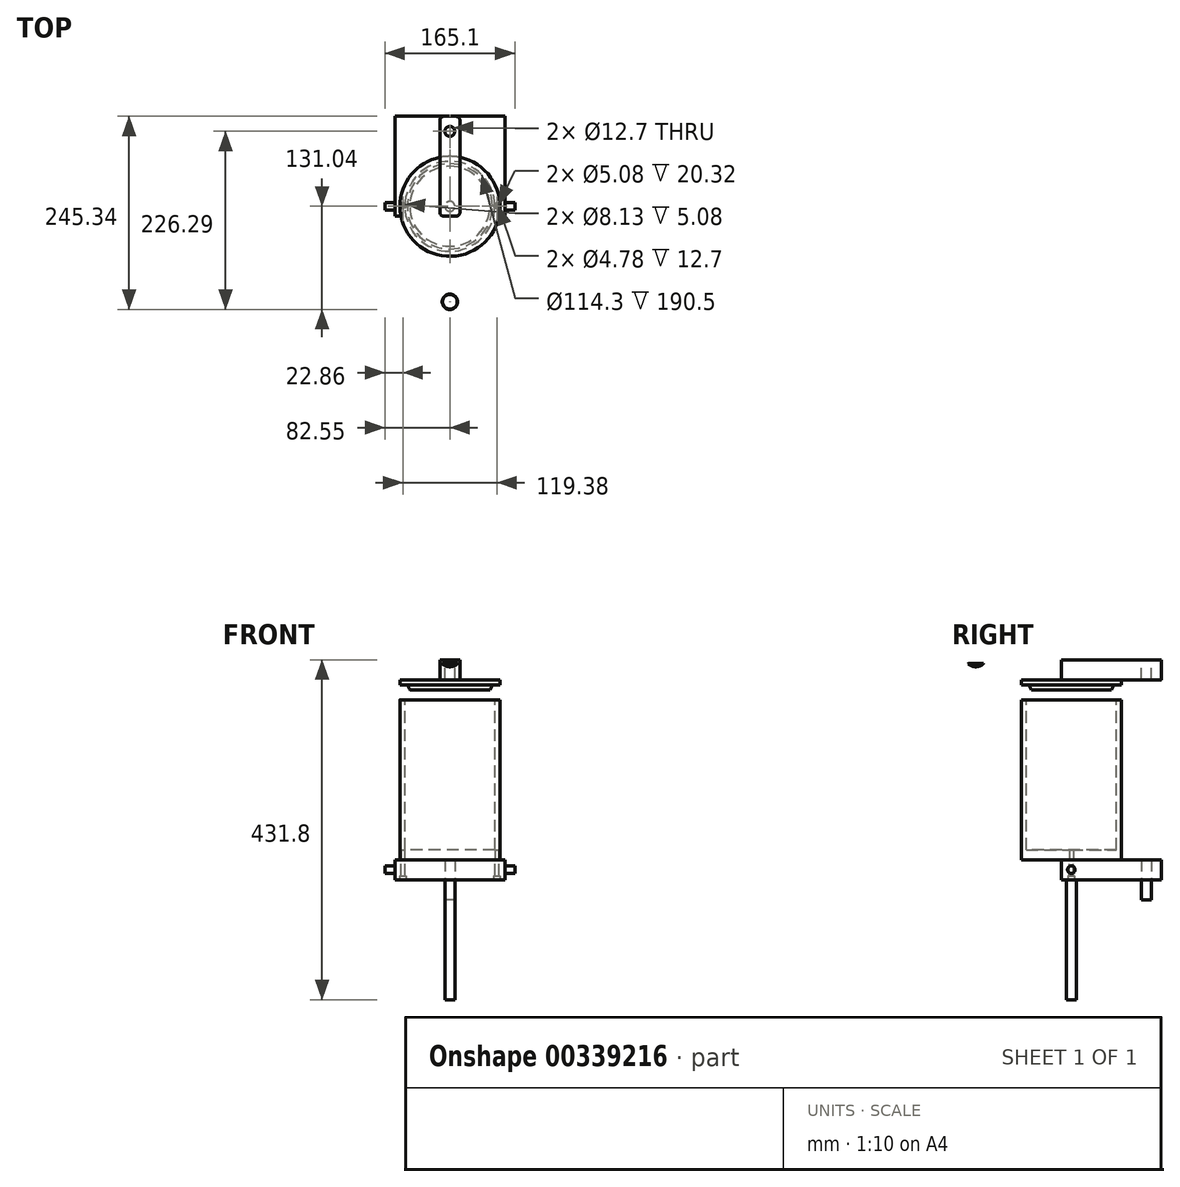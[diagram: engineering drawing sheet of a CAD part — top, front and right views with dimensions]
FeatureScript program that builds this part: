
annotation { "Feature Type Name" : "Feature", "Feature Type Description" : "" }
export const myFeature = defineFeature(function(context is Context, id is Id, definition is map)
    precondition{}
    {
        {
            var Q0;
            Q0=qCreatedBy(makeId("Top.planeOp"),FACE);
            var sketch = newSketch(context, id + "F0", { "sketchPlane" : qUnion([Q0])});
            skCircle(sketch, "E0", {"center": v(0, 0) * mm, "radius": 63.5 * mm});
            skSolve(sketch);
        }
        {
            var Q0;
            Q0=qSketchRegion(id+"F0",true);
            extrude(context, id + "F1", {"entities" : qUnion([Q0]), "depth" : 203.2 * mm});
        }
        {
            var Q0;
            Q0=makeQuery(id+"F1.opExtrude","CAP_FACE",FACE,{"disambiguationData":[OSD([sQuery(id+"F0.wireOp",EDGE,"E0")])],"isStart":false});
            var sketch = newSketch(context, id + "F2", { "sketchPlane" : qUnion([Q0])});
            skCircle(sketch, "E1", {"center": v(0, 0) * mm, "radius": 57.15 * mm});
            skSolve(sketch);
        }
        {
            var Q0;
            Q0=qSketchRegion(id+"F2",true);
            extrude(context, id + "F3", {"entities" : qUnion([Q0]), "operationType" : NewBodyOperationType.REMOVE, "oppositeDirection" : true, "depth" : 190.5 * mm});
        }
        {
            var Q0;
            Q0=qCreatedBy(makeId("Top.planeOp"),FACE);
            cPlane(context, id + "F4", {"entities" : qUnion([Q0]), "cplaneType" : CPlaneType.OFFSET, "offset" : 254 * mm, "width" : 152.4 * mm, "height" : 152.4 * mm});
        }
        {
            var Q0;
            Q0=qCreatedBy(makeId("Front.planeOp"),FACE);
            var sketch = newSketch(context, id + "F5", { "sketchPlane" : qUnion([Q0])});
            skLineSegment(sketch, "E2", {"start": v(0, 228.6) * mm, "end": v(-63.5, 228.6) * mm});
            skLineSegment(sketch, "E3", {"start": v(-63.5, 228.6) * mm, "end": v(-63.5, 222.25) * mm});
            skLineSegment(sketch, "E4", {"start": v(-63.5, 222.25) * mm, "end": v(-54.11, 222.25) * mm});
            skLineSegment(sketch, "E5", {"start": v(-54.11, 222.25) * mm, "end": v(-50.8, 215.9) * mm});
            skLineSegment(sketch, "E6", {"start": v(-50.8, 215.9) * mm, "end": v(0, 215.9) * mm});
            skLineSegment(sketch, "E7", {"start": v(0, 215.9) * mm, "end": v(0, 228.6) * mm});
            skSolve(sketch);
        }
        {
            var Q0;
            Q0=qSketchRegion(id+"F5",true);
            var Q1;
            Q1=sQuery(id+"F5.wireOp",EDGE,"E7");
            revolve(context, id + "F6", {"entities" : qUnion([Q0]), "axis" : qUnion([Q1]), "revolveType" : RevolveType.FULL});
        }
        {
            var Q0;
            Q0=makeQuery(id+"F1.opExtrude","CAP_FACE",FACE,{"disambiguationData":[OSD([sQuery(id+"F0.wireOp",EDGE,"E0")])],"isStart":true});
            var sketch = newSketch(context, id + "F7", { "sketchPlane" : qUnion([Q0])});
            skCircle(sketch, "E8", {"center": v(-59.7, 0) * mm, "radius": 2.39 * mm});
            skCircle(sketch, "E9", {"center": v(59.7, 0) * mm, "radius": 2.39 * mm});
            skSolve(sketch);
        }
        {
            var Q0;
            Q0=qSketchRegion(id+"F7",true);
            extrude(context, id + "F8", {"entities" : qUnion([Q0]), "operationType" : NewBodyOperationType.REMOVE, "oppositeDirection" : true, "depth" : 12.7 * mm});
        }
        {
            var Q0;
            Q0=makeQuery(id+"F1.opExtrude","CAP_FACE",FACE,{"disambiguationData":[OSD([sQuery(id+"F0.wireOp",EDGE,"E0")])],"isStart":true});
            var sketch = newSketch(context, id + "F9", { "sketchPlane" : qUnion([Q0])});
            skLineSegment(sketch, "E10.bottom", {"start": v(69.85, 12.7) * mm, "end": v(-69.85, 12.7) * mm});
            skLineSegment(sketch, "E10.top", {"start": v(69.85, -12.7) * mm, "end": v(-69.85, -12.7) * mm});
            skLineSegment(sketch, "E10.left", {"start": v(69.85, 12.7) * mm, "end": v(69.85, -12.7) * mm});
            skLineSegment(sketch, "E10.right", {"start": v(-69.85, 12.7) * mm, "end": v(-69.85, -12.7) * mm});
            skPoint(sketch, "E10.middle", {"position": v(0, 0) * mm});
            skCircle(sketch, "E11", {"center": v(-59.7, 0) * mm, "radius": 2.54 * mm});
            skCircle(sketch, "E12", {"center": v(59.7, 0) * mm, "radius": 2.54 * mm});
            skSolve(sketch);
        }
        {
            var Q0;
            Q0=qSketchRegion(id+"F9",true);
            extrude(context, id + "F10", {"entities" : qUnion([Q0]), "depth" : 25.4 * mm});
        }
        {
            var Q0;
            Q0=makeQuery(id+"F10.opExtrude","CAP_FACE",FACE,{"disambiguationData":[OSD([sQuery(id+"F9.wireOp",EDGE,"E10.bottom"),sQuery(id+"F9.wireOp",EDGE,"E10.top"),sQuery(id+"F9.wireOp",EDGE,"E10.left"),sQuery(id+"F9.wireOp",EDGE,"E10.right"),sQuery(id+"F9.wireOp",EDGE,"E11"),sQuery(id+"F9.wireOp",EDGE,"E12")])],"isStart":false});
            var sketch = newSketch(context, id + "F11", { "sketchPlane" : qUnion([Q0])});
            skCircle(sketch, "E13", {"center": v(-59.7, 0) * mm, "radius": 4.06 * mm});
            skCircle(sketch, "E14", {"center": v(59.7, 0) * mm, "radius": 4.06 * mm});
            skSolve(sketch);
        }
        {
            var Q0;
            Q0=qSketchRegion(id+"F11",true);
            extrude(context, id + "F12", {"entities" : qUnion([Q0]), "operationType" : NewBodyOperationType.REMOVE, "oppositeDirection" : true, "depth" : 5.08 * mm});
        }
        {
            var Q0;
            Q0=makeQuery(id+"F10.opExtrude","SWEPT_FACE",FACE,{"disambiguationData":[OSD([sQuery(id+"F9.wireOp",EDGE,"E10.right")])]});
            var sketch = newSketch(context, id + "F13", { "sketchPlane" : qUnion([Q0])});
            skCircle(sketch, "E15", {"center": v(0, -12.7) * mm, "radius": 4.76 * mm});
            skSolve(sketch);
        }
        {
            var Q0;
            Q0=makeQuery(id+"F10.opExtrude","CAP_FACE",FACE,{"disambiguationData":[OSD([sQuery(id+"F9.wireOp",EDGE,"E10.bottom"),sQuery(id+"F9.wireOp",EDGE,"E10.top"),sQuery(id+"F9.wireOp",EDGE,"E10.left"),sQuery(id+"F9.wireOp",EDGE,"E10.right"),sQuery(id+"F9.wireOp",EDGE,"E11"),sQuery(id+"F9.wireOp",EDGE,"E12")])],"isStart":false});
            var sketch = newSketch(context, id + "F14", { "sketchPlane" : qUnion([Q0])});
            skCircle(sketch, "E16", {"center": v(0, 0) * mm, "radius": 6.35 * mm});
            skSolve(sketch);
        }
        {
            var Q0;
            Q0=qSketchRegion(id+"F14",true);
            extrude(context, id + "F15", {"entities" : qUnion([Q0]), "depth" : 152.4 * mm});
        }
        {
            var Q0;
            Q0=makeQuery(id+"F6.opRevolve","SWEPT_FACE",FACE,{"disambiguationData":[OSD([sQuery(id+"F5.wireOp",EDGE,"E2")])]});
            var sketch = newSketch(context, id + "F16", { "sketchPlane" : qUnion([Q0])});
            skLineSegment(sketch, "E17.bottom", {"start": v(12.7, -12.7) * mm, "end": v(-12.7, -12.7) * mm});
            skLineSegment(sketch, "E17.top", {"start": v(12.7, 114.3) * mm, "end": v(-12.7, 114.3) * mm});
            skLineSegment(sketch, "E17.left", {"start": v(12.7, -12.7) * mm, "end": v(12.7, 114.3) * mm});
            skLineSegment(sketch, "E17.right", {"start": v(-12.7, -12.7) * mm, "end": v(-12.7, 114.3) * mm});
            skSolve(sketch);
        }
        {
            var Q0;
            Q0=qSketchRegion(id+"F16",true);
            extrude(context, id + "F17", {"entities" : qUnion([Q0]), "depth" : 25.4 * mm});
        }
        {
            var Q0;
            Q0=makeQuery(id+"F17.opExtrude","CAP_FACE",FACE,{"disambiguationData":[OSD([sQuery(id+"F16.wireOp",EDGE,"E17.bottom"),sQuery(id+"F16.wireOp",EDGE,"E17.top"),sQuery(id+"F16.wireOp",EDGE,"E17.left"),sQuery(id+"F16.wireOp",EDGE,"E17.right")])],"isStart":false});
            var sketch = newSketch(context, id + "F18", { "sketchPlane" : qUnion([Q0])});
            skCircle(sketch, "E18", {"center": v(0, 95.25) * mm, "radius": 6.35 * mm});
            skSolve(sketch);
        }
        {
            var Q0;
            Q0=qSketchRegion(id+"F18",true);
            extrude(context, id + "F19", {"entities" : qUnion([Q0]), "operationType" : NewBodyOperationType.REMOVE, "oppositeDirection" : true, "depth" : 25.4 * mm});
        }
        {
            var Q0;
            Q0=qCreatedBy(id+"F4.planeOp",FACE);
            var sketch = newSketch(context, id + "F20", { "sketchPlane" : qUnion([Q0])});
            skCircle(sketch, "E19", {"center": v(0, 95.25) * mm, "radius": 6.35 * mm});
            skSolve(sketch);
        }
        {
            var Q0;
            Q0=qSketchRegion(id+"F20",true);
            extrude(context, id + "F21", {"entities" : qUnion([Q0]), "oppositeDirection" : true, "depth" : 304.8 * mm});
        }
        {
            var Q0;
            Q0=makeQuery(id+"F17.opExtrude","SWEPT_EDGE",EDGE,{"disambiguationData":[OSD([sQuery(id+"F16.wireOp",EDGE,"E17.bottom"),sQuery(id+"F16.wireOp",EDGE,"E17.right")])]});
            var Q1;
            Q1=makeQuery(id+"F17.opExtrude","SWEPT_EDGE",EDGE,{"disambiguationData":[OSD([sQuery(id+"F16.wireOp",EDGE,"E17.bottom"),sQuery(id+"F16.wireOp",EDGE,"E17.left")])]});
            var Q2;
            Q2=makeQuery(id+"F17.opExtrude","SWEPT_EDGE",EDGE,{"disambiguationData":[OSD([sQuery(id+"F16.wireOp",EDGE,"E17.top"),sQuery(id+"F16.wireOp",EDGE,"E17.left")])]});
            var Q3;
            Q3=makeQuery(id+"F17.opExtrude","SWEPT_EDGE",EDGE,{"disambiguationData":[OSD([sQuery(id+"F16.wireOp",EDGE,"E17.top"),sQuery(id+"F16.wireOp",EDGE,"E17.right")])]});
            fillet(context, id + "F22", {"entities" : qUnion([Q0, Q1, Q2, Q3]), "radius" : 5.08 * mm, "tangentPropagation" : true, "allowEdgeOverflow" : false});
        }
        {
            var Q0;
            Q0=makeQuery(id+"F10.opExtrude","SWEPT_FACE",FACE,{"disambiguationData":[OSD([sQuery(id+"F9.wireOp",EDGE,"E10.top")])]});
            var sketch = newSketch(context, id + "F23", { "sketchPlane" : qUnion([Q0])});
            skLineSegment(sketch, "E20.bottom", {"start": v(69.85, -25.4) * mm, "end": v(-69.85, -25.4) * mm});
            skLineSegment(sketch, "E20.top", {"start": v(69.85, 0) * mm, "end": v(-69.85, 0) * mm});
            skLineSegment(sketch, "E20.left", {"start": v(69.85, -25.4) * mm, "end": v(69.85, 0) * mm});
            skLineSegment(sketch, "E20.right", {"start": v(-69.85, -25.4) * mm, "end": v(-69.85, 0) * mm});
            skSolve(sketch);
        }
        {
            var Q0;
            Q0=qSketchRegion(id+"F23",true);
            extrude(context, id + "F24", {"entities" : qUnion([Q0]), "operationType" : NewBodyOperationType.ADD, "depth" : 101.6 * mm});
        }
        {
            var Q0;
            Q0=makeQuery(id+"F24.boolean.opBoolean","MERGE",FACE,{"derivedFrom":[makeQuery(id+"F10.opExtrude","CAP_FACE",FACE,{"disambiguationData":[OSD([sQuery(id+"F9.wireOp",EDGE,"E10.bottom"),sQuery(id+"F9.wireOp",EDGE,"E10.top"),sQuery(id+"F9.wireOp",EDGE,"E10.left"),sQuery(id+"F9.wireOp",EDGE,"E10.right"),sQuery(id+"F9.wireOp",EDGE,"E11"),sQuery(id+"F9.wireOp",EDGE,"E12")])],"isStart":false}),makeQuery(id+"F24.opExtrude","SWEPT_FACE",FACE,{"disambiguationData":[OSD([sQuery(id+"F23.wireOp",EDGE,"E20.bottom")])]})]});
            var sketch = newSketch(context, id + "F25", { "sketchPlane" : qUnion([Q0])});
            skCircle(sketch, "E21", {"center": v(0, -95.25) * mm, "radius": 6.35 * mm});
            skSolve(sketch);
        }
        {
            var Q0;
            Q0=qSketchRegion(id+"F25",true);
            extrude(context, id + "F26", {"entities" : qUnion([Q0]), "operationType" : NewBodyOperationType.REMOVE, "endBound" : BoundingType.THROUGH_ALL, "oppositeDirection" : true, "depth" : 25.4 * mm});
        }
        {
            var Q0;
            Q0=qCreatedBy(makeId("Right.planeOp"),FACE);
            var sketch = newSketch(context, id + "F27", { "sketchPlane" : qUnion([Q0])});
            skLineSegment(sketch, "E22", {"start": v(-121.3, 246.09) * mm, "end": v(-121.3, 245.07) * mm});
            skLineSegment(sketch, "E23", {"start": v(-130.74, 249.58) * mm, "end": v(-130.6, 249.58) * mm});
            skArc(sketch, "E24", {"start": v(-130.6, 249.58) * mm, "mid": v(-126.2, 247.15) * mm, "end": v(-121.3, 246.09) * mm});
            skPoint(sketch, "E24.second.point", {"position": v(-124.15, 246.52) * mm});
            skArc(sketch, "E25.0", {"start": v(-131.04, 248.65) * mm, "mid": v(-126.46, 246.17) * mm, "end": v(-121.37, 245.08) * mm});
            skLineSegment(sketch, "E26", {"start": v(-130.74, 249.58) * mm, "end": v(-131.04, 248.65) * mm});
            skLineSegment(sketch, "E27", {"start": v(-121.3, 245.07) * mm, "end": v(-121.37, 245.08) * mm});
            skSolve(sketch);
        }
        {
            var Q0;
            Q0=qSketchRegion(id+"F27",true);
            var Q1;
            Q1=sQuery(id+"F27.wireOp",EDGE,"E22");
            revolve(context, id + "F28", {"entities" : qUnion([Q0]), "axis" : qUnion([Q1]), "revolveType" : RevolveType.FULL});
        }
        {
            var Q0;
            Q0=qSketchRegion(id+"F13",true);
            var Q1;
            Q1=sQuery(id+"F13.wireOp",EDGE,"E15");
            extrude(context, id + "F29", {"entities" : qUnion([Q0]), "surfaceEntities" : qUnion([Q1]), "depth" : 12.7 * mm});
        }
        {
            var Q0;
            Q0=makeQuery(id+"F29.opExtrude","SWEPT_BODY",BODY,{"disambiguationData":[OSD([sQuery(id+"F13.wireOp",EDGE,"E15")])]});
            var Q1;
            Q1=qCreatedBy(makeId("Right.planeOp"),FACE);
            mirror(context, id + "F30", {"entities" : qUnion([Q0]), "mirrorPlane" : qUnion([Q1])});
        }
    });
